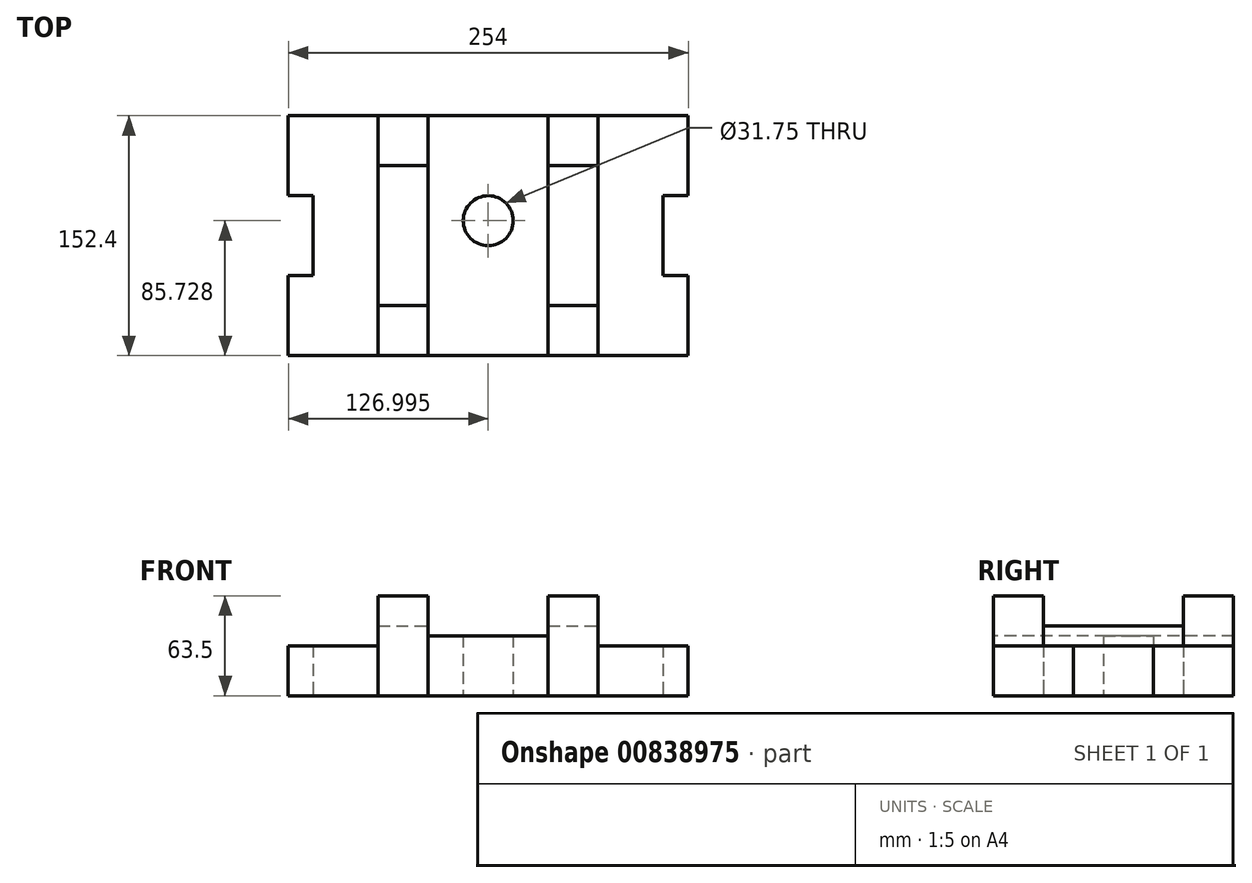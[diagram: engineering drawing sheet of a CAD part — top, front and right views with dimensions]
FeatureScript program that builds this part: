
annotation { "Feature Type Name" : "Feature", "Feature Type Description" : "" }
export const myFeature = defineFeature(function(context is Context, id is Id, definition is map)
    precondition{}
    {
        {
            var Q0;
            Q0=qCreatedBy(makeId("Top.planeOp"),FACE);
            var sketch = newSketch(context, id + "F0", { "sketchPlane" : qUnion([Q0])});
            skLineSegment(sketch, "E0", {"start": v(-139.03, 83.04) * mm, "end": v(114.97, 83.04) * mm});
            skLineSegment(sketch, "E1", {"start": v(114.97, 83.04) * mm, "end": v(114.97, 32.24) * mm});
            skLineSegment(sketch, "E2", {"start": v(114.97, 32.24) * mm, "end": v(99.1, 32.24) * mm});
            skLineSegment(sketch, "E3", {"start": v(99.1, 32.24) * mm, "end": v(99.1, -18.56) * mm});
            skLineSegment(sketch, "E4", {"start": v(99.1, -18.56) * mm, "end": v(114.97, -18.56) * mm});
            skLineSegment(sketch, "E5", {"start": v(114.97, -18.56) * mm, "end": v(114.97, -69.36) * mm});
            skLineSegment(sketch, "E6", {"start": v(114.97, -69.36) * mm, "end": v(-139.03, -69.36) * mm});
            skLineSegment(sketch, "E7", {"start": v(-139.03, -69.36) * mm, "end": v(-139.03, -18.56) * mm});
            skLineSegment(sketch, "E8", {"start": v(-139.03, -18.56) * mm, "end": v(-123.16, -18.56) * mm});
            skLineSegment(sketch, "E9", {"start": v(-123.16, -18.56) * mm, "end": v(-123.16, 32.24) * mm});
            skLineSegment(sketch, "E10", {"start": v(-123.16, 32.24) * mm, "end": v(-139.03, 32.24) * mm});
            skLineSegment(sketch, "E11", {"start": v(-139.03, 32.24) * mm, "end": v(-139.03, 83.04) * mm});
            skLineSegment(sketch, "E12", {"start": v(-81.88, 83.04) * mm, "end": v(-81.88, -69.36) * mm});
            skLineSegment(sketch, "E13", {"start": v(57.82, 83.04) * mm, "end": v(57.82, -69.36) * mm});
            skLineSegment(sketch, "E14", {"start": v(-50.13, 83.04) * mm, "end": v(-50.13, -69.36) * mm});
            skLineSegment(sketch, "E15", {"start": v(26.07, 83.04) * mm, "end": v(26.07, -69.36) * mm});
            skLineSegment(sketch, "E16", {"start": v(-81.88, 51.3) * mm, "end": v(-50.13, 51.3) * mm});
            skLineSegment(sketch, "E17", {"start": v(-81.88, -37.6) * mm, "end": v(-50.13, -37.6) * mm});
            skLineSegment(sketch, "E18", {"start": v(26.07, 51.3) * mm, "end": v(57.82, 51.3) * mm});
            skLineSegment(sketch, "E19", {"start": v(26.07, -37.6) * mm, "end": v(57.82, -37.6) * mm});
            skCircle(sketch, "E20", {"center": v(-12.03, 16.37) * mm, "radius": 15.88 * mm});
            skSolve(sketch);
        }
        {
            var Q0;
            {var subQ0=sQuery(id+"F0.wireOp",EDGE,"E7");Q0=makeQuery(id+"F0.imprint","IMPRINT",FACE,{"disambiguationData":[TD([[makeQuery(id+"F0.imprint","IMPRINT",EDGE,{"derivedFrom":subQ0}),-1.0]])]});}
            var Q1;
            {var subQ0=sQuery(id+"F0.wireOp",EDGE,"E1");Q1=makeQuery(id+"F0.imprint","IMPRINT",FACE,{"disambiguationData":[TD([[makeQuery(id+"F0.imprint","IMPRINT",EDGE,{"derivedFrom":subQ0}),-1.0]])]});}
            extrude(context, id + "F1", {"entities" : qUnion([Q0, Q1]), "depth" : 31.75 * mm, "offsetDistance" : 25.4 * mm});
        }
        {
            var Q0;
            Q0=makeQuery(id+"F0.imprint","IMPRINT",FACE,{"disambiguationData":[TD([[makeQuery(id+"F0.imprint","IMPRINT",EDGE,{"derivedFrom":sQuery(id+"F0.wireOp",EDGE,"E20")}),-1.0]])]});
            extrude(context, id + "F2", {"entities" : qUnion([Q0]), "depth" : 38.1 * mm, "offsetDistance" : 25.4 * mm});
        }
        {
            var Q0;
            {var subQ0=sQuery(id+"F0.wireOp",EDGE,"E16");Q0=makeQuery(id+"F0.imprint","IMPRINT",FACE,{"disambiguationData":[TD([[makeQuery(id+"F0.imprint","IMPRINT",EDGE,{"derivedFrom":subQ0}),-1.0]])]});}
            var Q1;
            {var subQ0=sQuery(id+"F0.wireOp",EDGE,"E18");Q1=makeQuery(id+"F0.imprint","IMPRINT",FACE,{"disambiguationData":[TD([[makeQuery(id+"F0.imprint","IMPRINT",EDGE,{"derivedFrom":subQ0}),-1.0]])]});}
            extrude(context, id + "F3", {"entities" : qUnion([Q0, Q1]), "depth" : 44.45 * mm, "offsetDistance" : 25.4 * mm});
        }
        {
            var Q0;
            {var subQ5=sQuery(id+"F0.wireOp",EDGE,"E16");Q0=makeQuery(id+"F0.imprint","IMPRINT",FACE,{"disambiguationData":[TD([[makeQuery(id+"F0.imprint","IMPRINT",EDGE,{"derivedFrom":subQ5}),1.0]])]});}
            var Q1;
            {var subQ5=sQuery(id+"F0.wireOp",EDGE,"E17");Q1=makeQuery(id+"F0.imprint","IMPRINT",FACE,{"disambiguationData":[TD([[makeQuery(id+"F0.imprint","IMPRINT",EDGE,{"derivedFrom":subQ5}),-1.0]])]});}
            var Q2;
            {var subQ5=sQuery(id+"F0.wireOp",EDGE,"E18");Q2=makeQuery(id+"F0.imprint","IMPRINT",FACE,{"disambiguationData":[TD([[makeQuery(id+"F0.imprint","IMPRINT",EDGE,{"derivedFrom":subQ5}),1.0]])]});}
            var Q3;
            {var subQ5=sQuery(id+"F0.wireOp",EDGE,"E19");Q3=makeQuery(id+"F0.imprint","IMPRINT",FACE,{"disambiguationData":[TD([[makeQuery(id+"F0.imprint","IMPRINT",EDGE,{"derivedFrom":subQ5}),-1.0]])]});}
            extrude(context, id + "F4", {"entities" : qUnion([Q0, Q1, Q2, Q3]), "depth" : 63.5 * mm, "offsetDistance" : 25.4 * mm});
        }
    });
